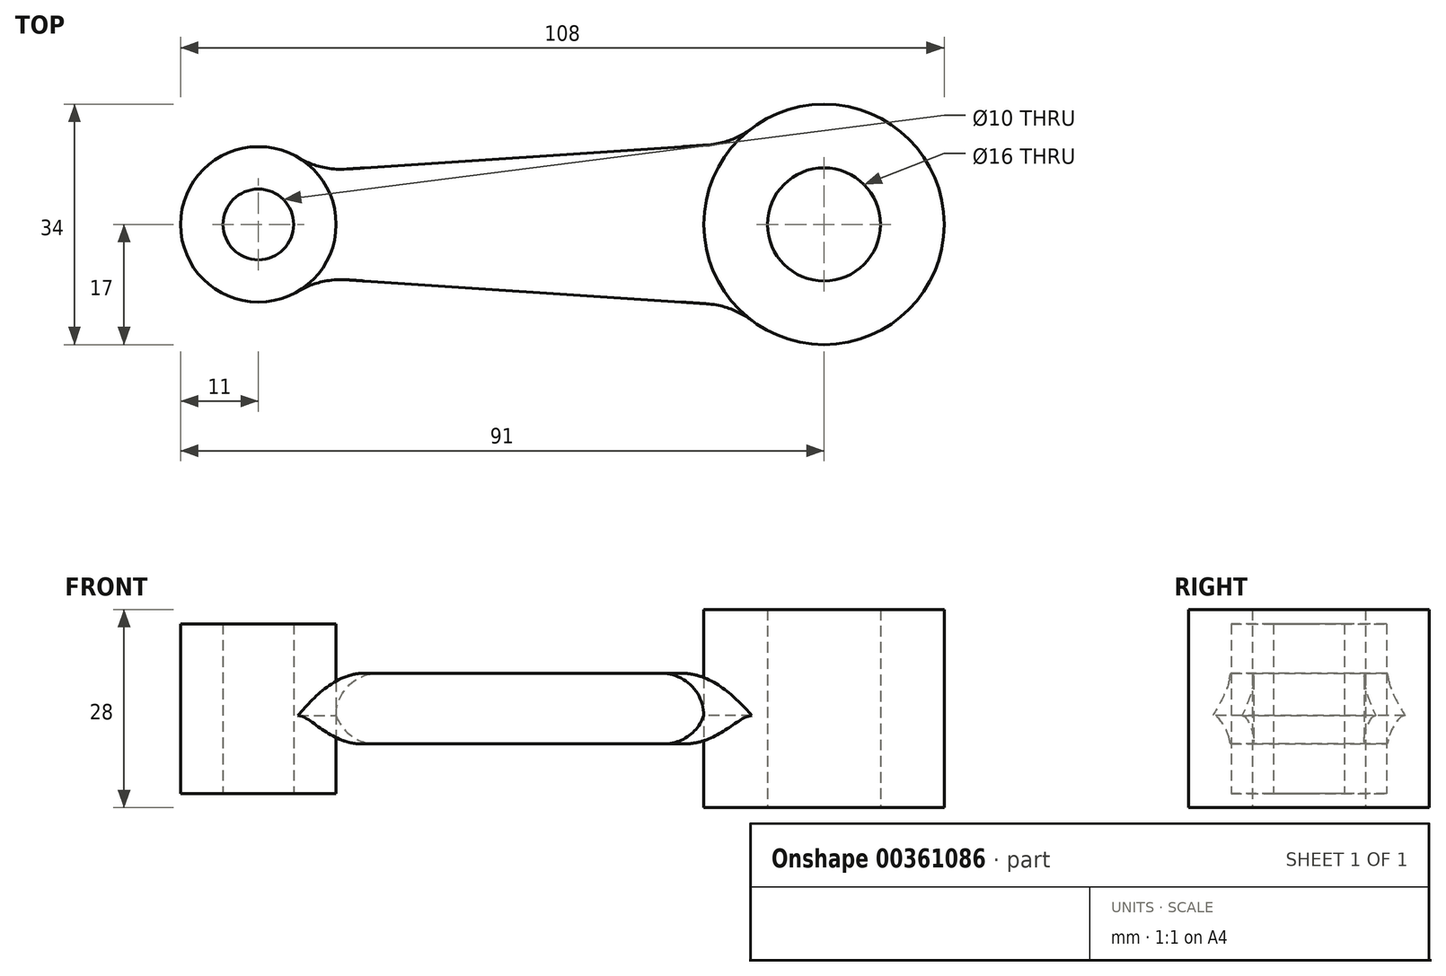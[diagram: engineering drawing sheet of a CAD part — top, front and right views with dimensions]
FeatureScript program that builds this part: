
annotation { "Feature Type Name" : "Feature", "Feature Type Description" : "" }
export const myFeature = defineFeature(function(context is Context, id is Id, definition is map)
    precondition{}
    {
        {
            var Q0;
            Q0=qCreatedBy(makeId("Top.planeOp"),FACE);
            var sketch = newSketch(context, id + "F0", { "sketchPlane" : qUnion([Q0])});
            skCircle(sketch, "E0", {"center": v(0, 0) * mm, "radius": 8 * mm});
            skLineSegment(sketch, "E1", {"start": v(0, 0) * mm, "end": v(-80, 0) * mm});
            skCircle(sketch, "E2", {"center": v(-80, 0) * mm, "radius": 5 * mm});
            skArc(sketch, "E3", {"start": v(-74.4, 9.47) * mm, "mid": v(-91, 0) * mm, "end": v(-74.4, -9.47) * mm});
            skArc(sketch, "E4", {"start": v(-10.2, -13.6) * mm, "mid": v(17, 0) * mm, "end": v(-10.2, 13.6) * mm});
            skLineSegment(sketch, "E5", {"start": v(0, 0) * mm, "end": v(-20, 0) * mm});
            skLineSegment(sketch, "E6", {"start": v(-80, 0) * mm, "end": v(-65, 0) * mm});
            skLineSegment(sketch, "E7", {"start": v(-65, 0) * mm, "end": v(-65, 8) * mm});
            skLineSegment(sketch, "E8", {"start": v(-65, 0) * mm, "end": v(-65, -8) * mm});
            skLineSegment(sketch, "E9", {"start": v(-65, -8) * mm, "end": v(-20, -11) * mm});
            skLineSegment(sketch, "E10", {"start": v(-65, 8) * mm, "end": v(-20, 11) * mm});
            skLineSegment(sketch, "E11", {"start": v(-65, 8) * mm, "end": v(-67.5, 7.83) * mm});
            skLineSegment(sketch, "E12", {"start": v(-65, -8) * mm, "end": v(-67.5, -7.83) * mm});
            skPoint(sketch, "E13.orphan", {"position": v(-82.52, 6.83) * mm});
            skPoint(sketch, "E14.visualSharp", {"position": v(-71.99, 7.53) * mm});
            skArc(sketch, "E14.filletArc", {"start": v(-74.4, 9.47) * mm, "mid": v(-71.08, 8.13) * mm, "end": v(-67.5, 7.83) * mm});
            skPoint(sketch, "E15.orphan", {"position": v(-82.52, -6.83) * mm});
            skPoint(sketch, "E16.visualSharp", {"position": v(-71.99, -7.53) * mm});
            skArc(sketch, "E16.filletArc", {"start": v(-67.5, -7.83) * mm, "mid": v(-71.08, -8.13) * mm, "end": v(-74.4, -9.47) * mm});
            skLineSegment(sketch, "E17", {"start": v(-20, 11) * mm, "end": v(-16.6, 11.23) * mm});
            skLineSegment(sketch, "E18", {"start": v(-20, -11) * mm, "end": v(-16.6, -11.23) * mm});
            skPoint(sketch, "E19.visualSharp", {"position": v(-12.52, 11.5) * mm});
            skArc(sketch, "E19.filletArc", {"start": v(-16.6, 11.23) * mm, "mid": v(-13.23, 11.95) * mm, "end": v(-10.2, 13.6) * mm});
            skPoint(sketch, "E20.visualSharp", {"position": v(-12.52, -11.5) * mm});
            skArc(sketch, "E20.filletArc", {"start": v(-10.2, -13.6) * mm, "mid": v(-13.23, -11.95) * mm, "end": v(-16.6, -11.23) * mm});
            skCircle(sketch, "E21", {"center": v(-80, 0) * mm, "radius": 11 * mm});
            skCircle(sketch, "E22", {"center": v(0, 0) * mm, "radius": 17 * mm});
            skSolve(sketch);
        }
        {
            var Q0;
            Q0=makeQuery(id+"F0.imprint","IMPRINT",FACE,{"disambiguationData":[TD([[makeQuery(id+"F0.imprint","IMPRINT",EDGE,{"derivedFrom":sQuery(id+"F0.wireOp",EDGE,"E0")}),-1.0]])]});
            extrude(context, id + "F1", {"entities" : qUnion([Q0]), "endBound" : BoundingType.SYMMETRIC, "depth" : 28 * mm});
        }
        {
            var Q0;
            Q0=makeQuery(id+"F0.imprint","IMPRINT",FACE,{"disambiguationData":[TD([[makeQuery(id+"F0.imprint","IMPRINT",EDGE,{"derivedFrom":sQuery(id+"F0.wireOp",EDGE,"E2")}),-1.0]])]});
            extrude(context, id + "F2", {"entities" : qUnion([Q0]), "endBound" : BoundingType.SYMMETRIC, "depth" : 24 * mm});
        }
        {
            var Q0;
            {var subQ1=sQuery(id+"F0.wireOp",EDGE,"E1");Q0=makeQuery(id+"F0.imprint","IMPRINT",FACE,{"disambiguationData":[TD([[makeQuery(id+"F0.imprint","IMPRINT",EDGE,{"derivedFrom":subQ1}),-1.0]])]});}
            var Q1;
            {var subQ1=sQuery(id+"F0.wireOp",EDGE,"E7");Q1=makeQuery(id+"F0.imprint","IMPRINT",FACE,{"disambiguationData":[TD([[makeQuery(id+"F0.imprint","IMPRINT",EDGE,{"derivedFrom":subQ1}),1.0]])]});}
            var Q2;
            {var subQ1=sQuery(id+"F0.wireOp",EDGE,"E8");Q2=makeQuery(id+"F0.imprint","IMPRINT",FACE,{"disambiguationData":[TD([[makeQuery(id+"F0.imprint","IMPRINT",EDGE,{"derivedFrom":subQ1}),-1.0]])]});}
            var Q3;
            {var subQ1=sQuery(id+"F0.wireOp",EDGE,"E1");Q3=makeQuery(id+"F0.imprint","IMPRINT",FACE,{"disambiguationData":[TD([[makeQuery(id+"F0.imprint","IMPRINT",EDGE,{"derivedFrom":subQ1}),1.0]])]});}
            extrude(context, id + "F3", {"entities" : qUnion([Q0, Q1, Q2, Q3]), "endBound" : BoundingType.SYMMETRIC, "depth" : 10 * mm});
        }
        {
            var Q0;
            Q0=makeQuery(id+"F3.opExtrude","CAP_EDGE",EDGE,{"disambiguationData":[OSD([sQuery(id+"F0.wireOp",EDGE,"E21")])],"isStart":false});
            fillet(context, id + "F4", {"entities" : qUnion([Q0]), "radius" : 6 * mm, "tangentPropagation" : true, "allowEdgeOverflow" : false});
        }
        {
            var Q0;
            Q0=makeQuery(id+"F3.opExtrude","CAP_EDGE",EDGE,{"disambiguationData":[OSD([sQuery(id+"F0.wireOp",EDGE,"E21")])],"isStart":true});
            fillet(context, id + "F5", {"entities" : qUnion([Q0]), "radius" : 6 * mm, "tangentPropagation" : true, "allowEdgeOverflow" : false});
        }
        {
            var Q0;
            Q0=makeQuery(id+"F3.opExtrude","CAP_EDGE",EDGE,{"disambiguationData":[OSD([sQuery(id+"F0.wireOp",EDGE,"E22")])],"isStart":false});
            fillet(context, id + "F6", {"entities" : qUnion([Q0]), "radius" : 6 * mm, "tangentPropagation" : true, "allowEdgeOverflow" : false});
        }
        {
            var Q0;
            Q0=makeQuery(id+"F3.opExtrude","CAP_EDGE",EDGE,{"disambiguationData":[OSD([sQuery(id+"F0.wireOp",EDGE,"E22")])],"isStart":true});
            fillet(context, id + "F7", {"entities" : qUnion([Q0]), "radius" : 6 * mm, "tangentPropagation" : true, "allowEdgeOverflow" : false});
        }
    });
